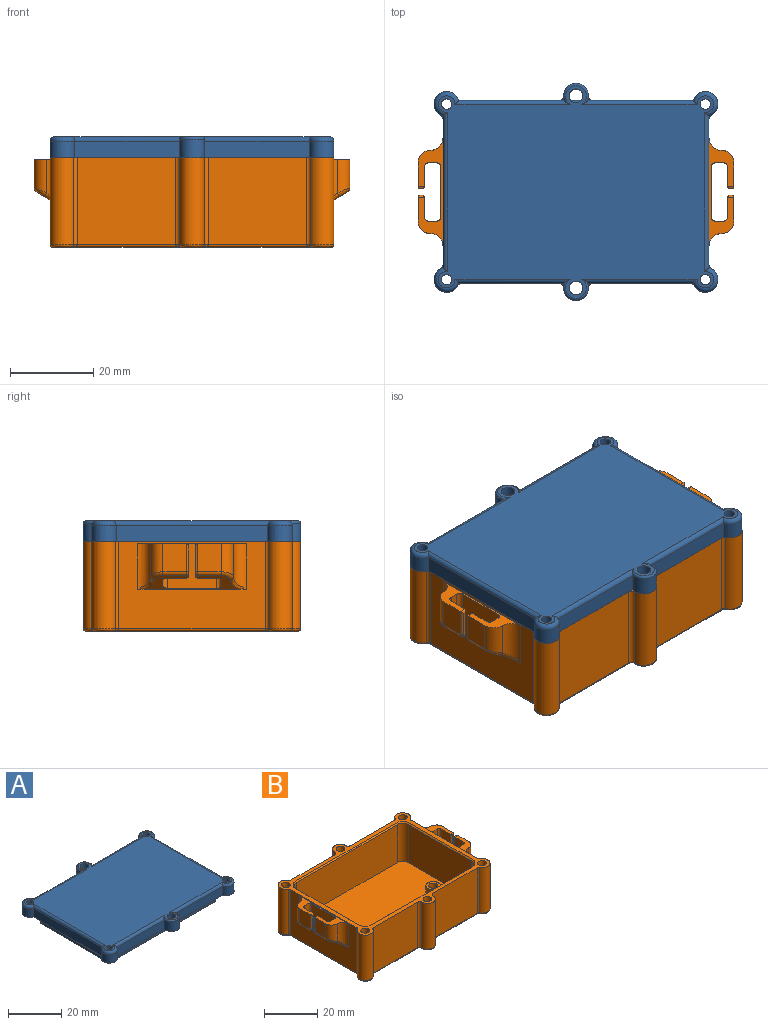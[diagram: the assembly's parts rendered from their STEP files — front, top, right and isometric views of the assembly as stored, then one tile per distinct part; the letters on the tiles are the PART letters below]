
ASSEMBLY  parts=2 mates=1
PART A: 52 faces, bbox 68.7x52.7x9.2 mm
  f0: cylinder r=3mm len=6mm, axis (0,0,-1), area 52.8mm2, adj f3,f4,f5,f6,f7,f41
  f1: cylinder r=1.65mm len=5mm, axis (0,0,-1), area 51.8mm2, adj f2,f3
  f2: plane 66.24x51.24mm, normal (0,0,1), area 2644.8mm2, adj f1,f4,f5,f9,f12,f13,f22,f23
  f3: plane 68.24x52.24mm, normal (0,0,-1), area 958.2mm2, adj f0,f1,f6,f7,f8,f9,f11,f14
  f4: cylinder r=1mm len=27.8mm, axis (-1,0,0), area 41.1mm2, adj f0,f2,f6,f35,f41
  f5: cylinder r=1mm len=27.8mm, axis (-1,0,0), area 41.1mm2, adj f0,f2,f7,f37,f41
  f6: plane 25.47x4mm, normal (0,-1,0), area 101.9mm2, adj f0,f3,f4,f18
  f7: plane 25.47x4mm, normal (0,-1,0), area 101.9mm2, adj f0,f3,f5,f19
  f8: cylinder r=3mm len=6mm, axis (0,0,-1), area 52.8mm2, adj f3,f12,f13,f14,f15,f40
  f9: cylinder r=1.65mm len=5mm, axis (0,0,-1), area 39mm2, adj f2,f3,f10,f11
  f10: cylinder r=1mm len=2.42mm, axis (1,0,0), area 2.1mm2, adj f9,f11
  f11: plane 4x2.42mm, normal (0,1,0), area 9.7mm2, adj f3,f9,f10
  f12: cylinder r=1mm len=27.8mm, axis (1,0,0), area 41.1mm2, adj f2,f8,f15,f38,f40
  f13: cylinder r=1mm len=27.8mm, axis (1,0,0), area 41.1mm2, adj f2,f8,f14,f36,f40
  f14: plane 25.47x4mm, normal (0,1,0), area 101.9mm2, adj f3,f8,f13,f16
  f15: plane 25.47x4mm, normal (0,1,0), area 101.9mm2, adj f3,f8,f12,f21
  f16: cylinder r=3mm len=5.87mm, axis (0,0,-1), area 49.4mm2, adj f3,f14,f17,f36
  f17: plane 36.51x4mm, normal (-1,0,0), area 146mm2, adj f3,f16,f18,f34
  f18: cylinder r=3mm len=5.87mm, axis (0,0,-1), area 49.4mm2, adj f3,f6,f17,f35
  f19: cylinder r=3mm len=5.87mm, axis (0,0,-1), area 49.4mm2, adj f3,f7,f20,f37
  f20: plane 36.51x4mm, normal (1,0,0), area 146mm2, adj f3,f19,f21,f39
  f21: cylinder r=3mm len=5.87mm, axis (0,0,-1), area 49.4mm2, adj f3,f15,f20,f38
  f22: cylinder r=1.25mm len=5mm, axis (0,0,1), area 39.3mm2, adj f2,f3
  f23: cylinder r=1.25mm len=5mm, axis (0,0,1), area 39.3mm2, adj f2,f3
  f24: cylinder r=1.25mm len=5mm, axis (0,0,1), area 39.3mm2, adj f2,f3
  f25: cylinder r=1.25mm len=5mm, axis (0,0,1), area 39.3mm2, adj f2,f3
  f26: plane 53.49x3.2mm, normal (0,1,0), area 171.2mm2, adj f3,f27,f33,f51
  f27: cylinder r=0.75mm len=3.2mm, axis (0,0,1), area 3.8mm2, adj f3,f26,f28,f51
  f28: plane 33.5x3.2mm, normal (-1,0,0), area 107.2mm2, adj f3,f27,f29,f51
  f29: cylinder r=0.75mm len=3.2mm, axis (0,0,1), area 3.8mm2, adj f3,f28,f30,f51
  f30: plane 53.49x3.2mm, normal (0,-1,0), area 171.2mm2, adj f3,f29,f31,f51
  f31: cylinder r=0.75mm len=3.2mm, axis (0,0,1), area 3.8mm2, adj f3,f30,f32,f51
  f32: plane 33.5x3.2mm, normal (1,0,0), area 107.2mm2, adj f3,f31,f33,f51
  f33: cylinder r=0.75mm len=3.2mm, axis (0,0,1), area 3.8mm2, adj f3,f26,f32,f51
  f34: cylinder r=1mm len=38.25mm, axis (0,1,0), area 58.3mm2, adj f2,f17,f35,f36
  f35: torus R=2mm, axis (0,0,1), area 17.9mm2, adj f2,f4,f18,f34
  f36: torus R=2mm, axis (0,0,1), area 17.9mm2, adj f2,f13,f16,f34
  f37: torus R=2mm, axis (0,0,1), area 17.9mm2, adj f2,f5,f19,f39
  f38: torus R=2mm, axis (0,0,1), area 17.9mm2, adj f2,f12,f21,f39
  f39: cylinder r=1mm len=38.25mm, axis (0,-1,0), area 58.3mm2, adj f2,f20,f37,f38
  f40: torus R=2.5mm, axis (0,0,1), area 9.7mm2, adj f2,f8,f12,f13
  f41: torus R=2.5mm, axis (0,0,1), area 9.7mm2, adj f0,f2,f4,f5
  f42: cylinder r=2.25mm len=2.25mm, axis (0,0,1), area 3.5mm2, adj f43,f49,f50,f51
  f43: plane 53.49x1mm, normal (0,1,0), area 53.5mm2, adj f42,f44,f50,f51
  f44: cylinder r=2.25mm len=2.25mm, axis (0,0,1), area 3.5mm2, adj f43,f45,f50,f51
  f45: plane 33.5x1mm, normal (1,0,0), area 33.5mm2, adj f44,f46,f50,f51
  f46: cylinder r=2.25mm len=2.25mm, axis (0,0,1), area 3.5mm2, adj f45,f47,f50,f51
  f47: plane 53.49x1mm, normal (0,-1,0), area 53.5mm2, adj f46,f48,f50,f51
  f48: cylinder r=2.25mm len=2.25mm, axis (0,0,1), area 3.5mm2, adj f47,f49,f50,f51
  f49: plane 33.5x1mm, normal (-1,0,0), area 33.5mm2, adj f42,f48,f50,f51
  f50: plane 57.99x38mm, normal (0,0,-1), area 2199.4mm2, adj f42,f43,f44,f45,f46,f47,f48,f49
  f51: plane 57.99x38mm, normal (0,0,1), area 275.1mm2, adj f26,f27,f28,f29,f30,f31,f32,f33
PART B: 180 faces, bbox 76.4x53x21.8 mm
  f0: plane 59.5x39.5mm, normal (0,0,1), area 2236.1mm2, adj f26,f27,f28,f29,f30,f31,f32,f33
  f1: plane 6.75x5.75mm, normal (1,0,0), area 38.8mm2, adj f2,f4,f97,f122
  f2: cylinder r=1mm len=5.75mm, axis (0,1,0), area 5.9mm2, adj f1,f5,f106,f121
  f3: plane 8.23x4.75mm, normal (-1,0,0), area 39.1mm2, adj f4,f5,f115,f118
  f4: plane 26x6mm, normal (0,0,1), area 61.1mm2, adj f1,f3,f7,f96,f97,f98,f99,f100
  f5: plane 22.47x5.78mm, normal (0.52,0,-0.85), area 52mm2, adj f2,f3,f7,f103,f104,f105,f106,f107
  f6: plane 0.5x0.04mm, normal (0,0,-1), area 0mm2, adj f7,f98,f102
  f7: plane 35.27x21.09mm, normal (1,0,0), area 453.1mm2, adj f4,f5,f6,f20,f95,f98,f100,f101
  f8: plane 6.75x5.75mm, normal (-1,0,0), area 38.8mm2, adj f9,f10,f17,f90
  f9: plane 26x6mm, normal (0,0,1), area 61.1mm2, adj f8,f11,f14,f15,f16,f17,f18,f25
  f10: cylinder r=1mm len=5.75mm, axis (0,-1,0), area 5.9mm2, adj f8,f12,f71,f92
  f11: plane 8.23x4.75mm, normal (1,0,0), area 39.1mm2, adj f9,f12,f78,f93
  f12: plane 22.47x5.78mm, normal (-0.52,0,-0.85), area 52mm2, adj f10,f11,f25,f70,f71,f72,f73,f74
  f13: plane 0.5x0.04mm, normal (0,0,-1), area 0mm2, adj f16,f25,f68
  f14: plane 6.75x5.75mm, normal (-1,0,0), area 38.8mm2, adj f9,f15,f72,f89
  f15: cylinder r=3mm len=7.98mm, axis (0,0,1), area 34.7mm2, adj f9,f14,f16,f73
  f16: cylinder r=3mm len=11mm, axis (0,0,-1), area 45.3mm2, adj f9,f13,f15,f25,f68,f74
  f17: cylinder r=3mm len=7.98mm, axis (0,0,-1), area 34.7mm2, adj f8,f9,f18,f71
  f18: cylinder r=3mm len=11mm, axis (0,0,1), area 45.3mm2, adj f9,f17,f25,f67,f69,f70
  f19: plane 67.24x51.24mm, normal (0,0,-1), area 2612.8mm2, adj f51,f53,f54,f55,f56,f57,f58,f59
  f20: plane 68.24x52.24mm, normal (0,0,1), area 429mm2, adj f7,f21,f22,f23,f24,f25,f46,f47
  f21: plane 23.59x21mm, normal (0,-1,0), area 495.4mm2, adj f20,f143,f162,f170
  f22: plane 23.59x21mm, normal (0,1,0), area 495.4mm2, adj f20,f136,f160,f168
  f23: plane 23.59x21mm, normal (0,-1,0), area 495.4mm2, adj f20,f147,f176,f178
  f24: plane 23.59x21mm, normal (0,1,0), area 495.4mm2, adj f20,f140,f172,f174
  f25: plane 35.27x21.09mm, normal (-1,0,0), area 453.1mm2, adj f9,f12,f13,f16,f18,f20,f67,f68
  f26: plane 53.5x17.5mm, normal (0,-1,0), area 936.2mm2, adj f0,f27,f33,f153
  f27: cylinder r=3mm len=17.5mm, axis (0,0,1), area 82.5mm2, adj f0,f26,f28,f155
  f28: plane 33.5x17.5mm, normal (1,0,0), area 586.2mm2, adj f0,f27,f29,f154
  f29: cylinder r=3mm len=17.5mm, axis (0,0,1), area 82.5mm2, adj f0,f28,f30,f152
  f30: plane 53.5x17.5mm, normal (0,1,0), area 936.2mm2, adj f0,f29,f31,f150
  f31: cylinder r=3mm len=17.5mm, axis (0,0,1), area 82.5mm2, adj f0,f30,f32,f148
  f32: plane 33.5x17.5mm, normal (-1,0,0), area 586.2mm2, adj f0,f31,f33,f149
  f33: cylinder r=3mm len=17.5mm, axis (0,0,1), area 82.5mm2, adj f0,f26,f32,f151
  f34: cylinder r=2.75mm len=5.5mm, axis (0,0,-1), area 51.8mm2, adj f0,f35
  f35: plane 5.5x5.5mm, normal (0,0,1), area 15.2mm2, adj f34,f44
  f36: cylinder r=2.75mm len=5.5mm, axis (0,0,-1), area 51.8mm2, adj f0,f37
  f37: plane 5.5x5.5mm, normal (0,0,1), area 15.2mm2, adj f36,f42
  f38: cylinder r=2.75mm len=5.5mm, axis (0,0,-1), area 51.8mm2, adj f0,f39
  f39: plane 5.5x5.5mm, normal (0,0,1), area 15.2mm2, adj f38,f40
  f40: cylinder r=1.65mm len=3.3mm, axis (0,0,1), area 33.2mm2, adj f39,f41
  f41: plane 3.3x3.3mm, normal (0,0,1), area 8.6mm2, adj f40
  f42: cylinder r=1.65mm len=3.3mm, axis (0,0,1), area 33.2mm2, adj f37,f43
  f43: plane 3.3x3.3mm, normal (0,0,1), area 8.6mm2, adj f42
  f44: cylinder r=1.65mm len=3.3mm, axis (0,0,1), area 33.2mm2, adj f35,f45
  f45: plane 3.3x3.3mm, normal (0,0,1), area 8.6mm2, adj f44
  f46: cylinder r=3mm len=21mm, axis (0,0,1), area 235.3mm2, adj f20,f142,f156,f172
  f47: cylinder r=3mm len=21mm, axis (0,0,1), area 235.3mm2, adj f20,f137,f158,f160
  f48: cylinder r=3mm len=21mm, axis (0,0,1), area 235.3mm2, adj f20,f141,f162,f164
  f49: cylinder r=3mm len=21mm, axis (0,0,1), area 235.3mm2, adj f20,f146,f166,f176
  f50: cylinder r=3mm len=21mm, axis (0,0,1), area 201.7mm2, adj f20,f138,f168,f174
  f51: cylinder r=1.65mm len=21.5mm, axis (0,0,1), area 222.9mm2, adj f19,f20
  f52: cylinder r=3mm len=21mm, axis (0,0,1), area 201.7mm2, adj f20,f145,f170,f178
  f53: cylinder r=1.65mm len=21.5mm, axis (0,0,1), area 222.9mm2, adj f19,f20
  f54: cylinder r=1.65mm len=21.5mm, axis (0,0,1), area 222.9mm2, adj f19,f20
  f55: cylinder r=1.65mm len=21.5mm, axis (0,0,1), area 222.9mm2, adj f19,f20
  f56: cylinder r=1.65mm len=21.5mm, axis (0,0,1), area 222.9mm2, adj f19,f20
  f57: cylinder r=1.65mm len=21.5mm, axis (0,0,1), area 222.9mm2, adj f19,f20
  f58: cylinder r=4mm len=4mm, axis (0,0,-1), area 9.4mm2, adj f19,f59,f65,f66
  f59: plane 4x1.5mm, normal (1,0,0), area 6mm2, adj f19,f58,f60,f66
  f60: cylinder r=4mm len=4mm, axis (0,0,-1), area 9.4mm2, adj f19,f59,f61,f66
  f61: plane 4x1.5mm, normal (0,-1,0), area 6mm2, adj f19,f60,f62,f66
  f62: cylinder r=4mm len=4mm, axis (0,0,-1), area 9.4mm2, adj f19,f61,f63,f66
  f63: plane 4x1.5mm, normal (-1,0,0), area 6mm2, adj f19,f62,f64,f66
  f64: cylinder r=4mm len=4mm, axis (0,0,-1), area 9.4mm2, adj f19,f63,f65,f66
  f65: plane 4x1.5mm, normal (0,1,0), area 6mm2, adj f19,f58,f64,f66
  f66: plane 12x12mm, normal (0,0,-1), area 95.1mm2, adj f58,f59,f60,f61,f62,f63,f64,f65
  f67: plane 0.5x0.04mm, normal (0,0,-1), area 0mm2, adj f18,f25,f69
  f68: plane 0.6x0.05mm, normal (0,-1,0), area 0mm2, adj f13,f16,f25,f74
  f69: plane 0.6x0.05mm, normal (0,1,0), area 0mm2, adj f18,f25,f67,f70
  f70: bspline ~3.95x3.53mm, area 6.4mm2, adj f12,f18,f25,f69,f71
  f71: bspline ~3.52x3.18mm, area 5.2mm2, adj f10,f12,f17,f70
  f72: cylinder r=1mm len=5.75mm, axis (0,-1,0), area 5.9mm2, adj f12,f14,f73,f88
  f73: bspline ~3.52x3.05mm, area 5.2mm2, adj f12,f15,f72,f74
  f74: bspline ~4.68x3.74mm, area 6.4mm2, adj f12,f16,f25,f68,f73
  f75: plane 10.08x2mm, normal (0,-1,0), area 18.9mm2, adj f9,f12,f76,f82
  f76: cylinder r=1mm len=8.85mm, axis (0,0,1), area 13.4mm2, adj f9,f12,f75,f77
  f77: plane 8.23x4.75mm, normal (1,0,0), area 39.1mm2, adj f9,f12,f76,f85
  f78: cylinder r=1mm len=8.85mm, axis (0,0,1), area 13.4mm2, adj f9,f11,f12,f79
  f79: plane 10.08x2mm, normal (0,1,0), area 18.9mm2, adj f9,f12,f78,f80
  f80: cylinder r=1mm len=10.69mm, axis (0,0,1), area 16.3mm2, adj f9,f12,f79,f81
  f81: plane 12x10.69mm, normal (-1,0,0), area 128.3mm2, adj f9,f12,f80,f82
  f82: cylinder r=1mm len=10.69mm, axis (0,0,1), area 16.3mm2, adj f9,f12,f75,f81
  f83: plane 6.84x0.5mm, normal (0,1,0), area 3.3mm2, adj f90,f91,f92,f93,f94
  f84: plane 6.84x0.5mm, normal (0,-1,0), area 3.3mm2, adj f85,f86,f87,f88,f89
  f85: cylinder r=0.5mm len=8.23mm, axis (0,0,-1), area 5.9mm2, adj f77,f84,f86,f87
  f86: cylinder r=0.5mm len=1.29mm, axis (-0.85,0,0.52), area 0.7mm2, adj f12,f84,f85,f88
  f87: cylinder r=0.5mm len=1.5mm, axis (1,0,0), area 0.8mm2, adj f9,f84,f85,f89
  f88: torus R=0.5mm, axis (0,1,0), area 0.7mm2, adj f72,f84,f86,f89
  f89: cylinder r=0.5mm len=6.75mm, axis (0,0,1), area 5.1mm2, adj f14,f84,f87,f88
  f90: cylinder r=0.5mm len=6.75mm, axis (0,0,-1), area 5.1mm2, adj f8,f83,f91,f92
  f91: cylinder r=0.5mm len=1.5mm, axis (-1,0,0), area 0.8mm2, adj f9,f83,f90,f93
  f92: torus R=0.5mm, axis (0,1,0), area 0.7mm2, adj f10,f83,f90,f94
  f93: cylinder r=0.5mm len=8.23mm, axis (0,0,1), area 5.9mm2, adj f11,f83,f91,f94
  f94: cylinder r=0.5mm len=1.29mm, axis (0.85,0,-0.52), area 0.7mm2, adj f12,f83,f92,f93
  f95: plane 0.5x0.04mm, normal (0,0,-1), area 0mm2, adj f7,f100,f101
  f96: plane 6.75x5.75mm, normal (1,0,0), area 38.8mm2, adj f4,f99,f105,f124
  f97: cylinder r=3mm len=7.98mm, axis (0,0,-1), area 34.7mm2, adj f1,f4,f98,f106
  f98: cylinder r=3mm len=11mm, axis (0,0,-1), area 45.3mm2, adj f4,f6,f7,f97,f102,f107
  f99: cylinder r=3mm len=7.98mm, axis (0,0,1), area 34.7mm2, adj f4,f96,f100,f104
  f100: cylinder r=3mm len=11mm, axis (0,0,1), area 45.3mm2, adj f4,f7,f95,f99,f101,f103
  f101: plane 0.6x0.05mm, normal (0,1,0), area 0mm2, adj f7,f95,f100,f103
  f102: plane 0.6x0.05mm, normal (0,-1,0), area 0mm2, adj f6,f7,f98,f107
  f103: bspline ~3.95x3.53mm, area 6.4mm2, adj f5,f7,f100,f101,f104
  f104: bspline ~3.52x3.05mm, area 5.2mm2, adj f5,f99,f103,f105
  f105: cylinder r=1mm len=5.75mm, axis (0,1,0), area 5.9mm2, adj f5,f96,f104,f126
  f106: bspline ~3.57x3.52mm, area 5.2mm2, adj f2,f5,f97,f107
  f107: bspline ~4.68x3.74mm, area 6.4mm2, adj f5,f7,f98,f102,f106
  f108: plane 10.08x2mm, normal (0,-1,0), area 18.9mm2, adj f4,f5,f109,f115
  f109: cylinder r=1mm len=10.69mm, axis (0,0,1), area 16.3mm2, adj f4,f5,f108,f110
  f110: plane 12x10.69mm, normal (1,0,0), area 128.3mm2, adj f4,f5,f109,f111
  f111: cylinder r=1mm len=10.69mm, axis (0,0,1), area 16.3mm2, adj f4,f5,f110,f112
  f112: plane 10.08x2mm, normal (0,1,0), area 18.9mm2, adj f4,f5,f111,f113
  f113: cylinder r=1mm len=8.85mm, axis (0,0,1), area 13.4mm2, adj f4,f5,f112,f114
  f114: plane 8.23x4.75mm, normal (-1,0,0), area 39.1mm2, adj f4,f5,f113,f125
  f115: cylinder r=1mm len=8.85mm, axis (0,0,1), area 13.4mm2, adj f3,f4,f5,f108
  f116: plane 6.84x0.5mm, normal (0,-1,0), area 3.3mm2, adj f118,f119,f120,f121,f122
  f117: plane 6.84x0.5mm, normal (0,1,0), area 3.3mm2, adj f123,f124,f125,f126,f127
  f118: cylinder r=0.5mm len=8.23mm, axis (0,0,1), area 5.9mm2, adj f3,f116,f119,f120
  f119: cylinder r=0.5mm len=1.29mm, axis (-0.85,0,-0.52), area 0.7mm2, adj f5,f116,f118,f121
  f120: cylinder r=0.5mm len=1.5mm, axis (-1,0,0), area 0.8mm2, adj f4,f116,f118,f122
  f121: torus R=0.5mm, axis (0,-1,0), area 0.7mm2, adj f2,f116,f119,f122
  f122: cylinder r=0.5mm len=6.75mm, axis (0,0,-1), area 5.1mm2, adj f1,f116,f120,f121
  f123: cylinder r=0.5mm len=1.5mm, axis (1,0,0), area 0.8mm2, adj f4,f117,f124,f125
  f124: cylinder r=0.5mm len=6.75mm, axis (0,0,1), area 5.1mm2, adj f96,f117,f123,f126
  f125: cylinder r=0.5mm len=8.23mm, axis (0,0,-1), area 5.9mm2, adj f114,f117,f123,f127
  f126: torus R=0.5mm, axis (0,-1,0), area 0.7mm2, adj f105,f117,f124,f127
  f127: cylinder r=0.5mm len=1.29mm, axis (0.85,0,0.52), area 0.7mm2, adj f5,f117,f125,f126
  f128: plane 4x2mm, normal (1,0,0), area 8mm2, adj f0,f66,f129,f135
  f129: cylinder r=1mm len=2mm, axis (0,0,-1), area 3.1mm2, adj f0,f66,f128,f130
  f130: plane 4x2mm, normal (0,-1,0), area 8mm2, adj f0,f66,f129,f131
  f131: cylinder r=1mm len=2mm, axis (0,0,-1), area 3.1mm2, adj f0,f66,f130,f132
  f132: plane 4x2mm, normal (-1,0,0), area 8mm2, adj f0,f66,f131,f133
  f133: cylinder r=1mm len=2mm, axis (0,0,-1), area 3.1mm2, adj f0,f66,f132,f134
  f134: plane 4x2mm, normal (0,1,0), area 8mm2, adj f0,f66,f133,f135
  f135: cylinder r=1mm len=2mm, axis (0,0,-1), area 3.1mm2, adj f0,f66,f128,f134
  f136: cylinder r=0.5mm len=26.75mm, axis (-1,0,0), area 19.8mm2, adj f19,f22,f161,f169
  f137: torus R=2.5mm, axis (0,0,1), area 9mm2, adj f19,f47,f159,f161
  f138: torus R=2.5mm, axis (0,0,1), area 8.5mm2, adj f19,f50,f169,f175
  f139: cylinder r=0.5mm len=37.3mm, axis (0,1,0), area 28.5mm2, adj f7,f19,f159,f165
  f140: cylinder r=0.5mm len=26.75mm, axis (-1,0,0), area 19.8mm2, adj f19,f24,f173,f175
  f141: torus R=2.5mm, axis (0,0,1), area 9mm2, adj f19,f48,f163,f165
  f142: torus R=2.5mm, axis (0,0,1), area 9mm2, adj f19,f46,f157,f173
  f143: cylinder r=0.5mm len=26.75mm, axis (1,0,0), area 19.8mm2, adj f19,f21,f163,f171
  f144: cylinder r=0.5mm len=37.3mm, axis (0,-1,0), area 28.5mm2, adj f19,f25,f157,f167
  f145: torus R=2.5mm, axis (0,0,1), area 8.5mm2, adj f19,f52,f171,f179
  f146: torus R=2.5mm, axis (0,0,1), area 9mm2, adj f19,f49,f167,f177
  f147: cylinder r=0.5mm len=26.75mm, axis (1,0,0), area 19.8mm2, adj f19,f23,f177,f179
  f148: cone r=3mm half-angle=45deg, axis (0,0,1), area 3.6mm2, adj f20,f31,f149,f150
  f149: plane 33.5x0.5mm, normal (-0.71,0,0.71), area 23.7mm2, adj f20,f32,f148,f151
  f150: plane 53.5x0.5mm, normal (0,0.71,0.71), area 37.8mm2, adj f20,f30,f148,f152
  f151: cone r=3mm half-angle=45deg, axis (0,0,1), area 3.6mm2, adj f20,f33,f149,f153
  f152: cone r=3mm half-angle=45deg, axis (0,0,1), area 3.6mm2, adj f20,f29,f150,f154
  f153: plane 53.5x0.5mm, normal (0,-0.71,0.71), area 37.8mm2, adj f20,f26,f151,f155
  f154: plane 33.5x0.5mm, normal (0.71,0,0.71), area 23.7mm2, adj f20,f28,f152,f155
  f155: cone r=3mm half-angle=45deg, axis (0,0,1), area 3.6mm2, adj f20,f27,f153,f154
  f156: cylinder r=1mm len=21mm, axis (0,0,1), area 22.7mm2, adj f20,f25,f46,f157
  f157: bspline ~1.06x1.03mm, area 0.4mm2, adj f142,f144,f156
  f158: cylinder r=1mm len=21mm, axis (0,0,1), area 22.7mm2, adj f7,f20,f47,f159
  f159: bspline ~1.06x1.03mm, area 0.4mm2, adj f137,f139,f158
  f160: cylinder r=1mm len=21mm, axis (0,0,1), area 22.7mm2, adj f20,f22,f47,f161
  f161: bspline ~1.06x1.03mm, area 0.4mm2, adj f136,f137,f160
  f162: cylinder r=1mm len=21mm, axis (0,0,1), area 22.7mm2, adj f20,f21,f48,f163
  f163: bspline ~1.06x1.03mm, area 0.4mm2, adj f141,f143,f162
  f164: cylinder r=1mm len=21mm, axis (0,0,1), area 22.7mm2, adj f7,f20,f48,f165
  f165: bspline ~1.06x1.03mm, area 0.4mm2, adj f139,f141,f164
  f166: cylinder r=1mm len=21mm, axis (0,0,1), area 22.7mm2, adj f20,f25,f49,f167
  f167: bspline ~1.06x1.03mm, area 0.4mm2, adj f144,f146,f166
  f168: cylinder r=1mm len=21mm, axis (0,0,1), area 33.6mm2, adj f20,f22,f50,f169
  f169: bspline ~2.1x1.53mm, area 0.7mm2, adj f136,f138,f168
  f170: cylinder r=1mm len=21mm, axis (0,0,1), area 33.6mm2, adj f20,f21,f52,f171
  f171: bspline ~2.1x1.53mm, area 0.7mm2, adj f143,f145,f170
  f172: cylinder r=1mm len=21mm, axis (0,0,1), area 22.7mm2, adj f20,f24,f46,f173
  f173: bspline ~1.06x1.03mm, area 0.4mm2, adj f140,f142,f172
  f174: cylinder r=1mm len=21mm, axis (0,0,1), area 33.6mm2, adj f20,f24,f50,f175
  f175: bspline ~2.1x1.53mm, area 0.7mm2, adj f138,f140,f174
  f176: cylinder r=1mm len=21mm, axis (0,0,1), area 22.7mm2, adj f20,f23,f49,f177
  f177: bspline ~1.06x1.03mm, area 0.4mm2, adj f146,f147,f176
  f178: cylinder r=1mm len=21mm, axis (0,0,1), area 33.6mm2, adj f20,f23,f52,f179
  f179: bspline ~2.1x1.53mm, area 0.7mm2, adj f145,f147,f178
PLACE A t=(-36.08,-15.58,-2.35)mm
PLACE B t=(-36.08,-15.58,-2.35)mm
MATE fastened B.f48 <-> A.f19  axis (0,0,1) through (-4.96,-36.7,19.15)mm
